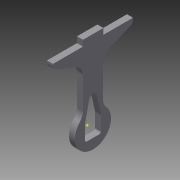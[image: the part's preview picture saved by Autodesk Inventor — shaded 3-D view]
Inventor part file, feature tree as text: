
AUTODESK INVENTOR PART (.ipt)
format: ipt  version: 2013 (Build 170138000, 138)  size: 131,072 bytes
history: native  units: mm
features: extrude x1, sketch x1
ambient origin geometry x8: Origin, YZ Plane, XZ Plane, XY Plane, X Axis, Y Axis, Z Axis, Center Point
feature tree (2):
  extrude  "Extrusion6"  Depth=3.0mm
  sketch  "Sketch1"  dims[d8=22.5deg d16=3.0mm d25=10.0mm d32=6.0mm d33=6.0mm d68=18.0mm d69=6.0mm d70=38.0mm d74=22.5deg d75=8.0mm d76=8.0mm d77=4.0mm d78=13.0mm d79=6.0mm d80=1.0mm d81=90.0mm d82=46.0mm d84=38.0mm d85=3.0mm d86=5.0mm d87=20.0mm d88=40.0mm d90=2.0mm d93=1.0mm d94=1.0mm d95=22.5deg d96=22.5deg d97=4.0mm d98=4.0mm d101=3.0mm d102=0.0mm]
